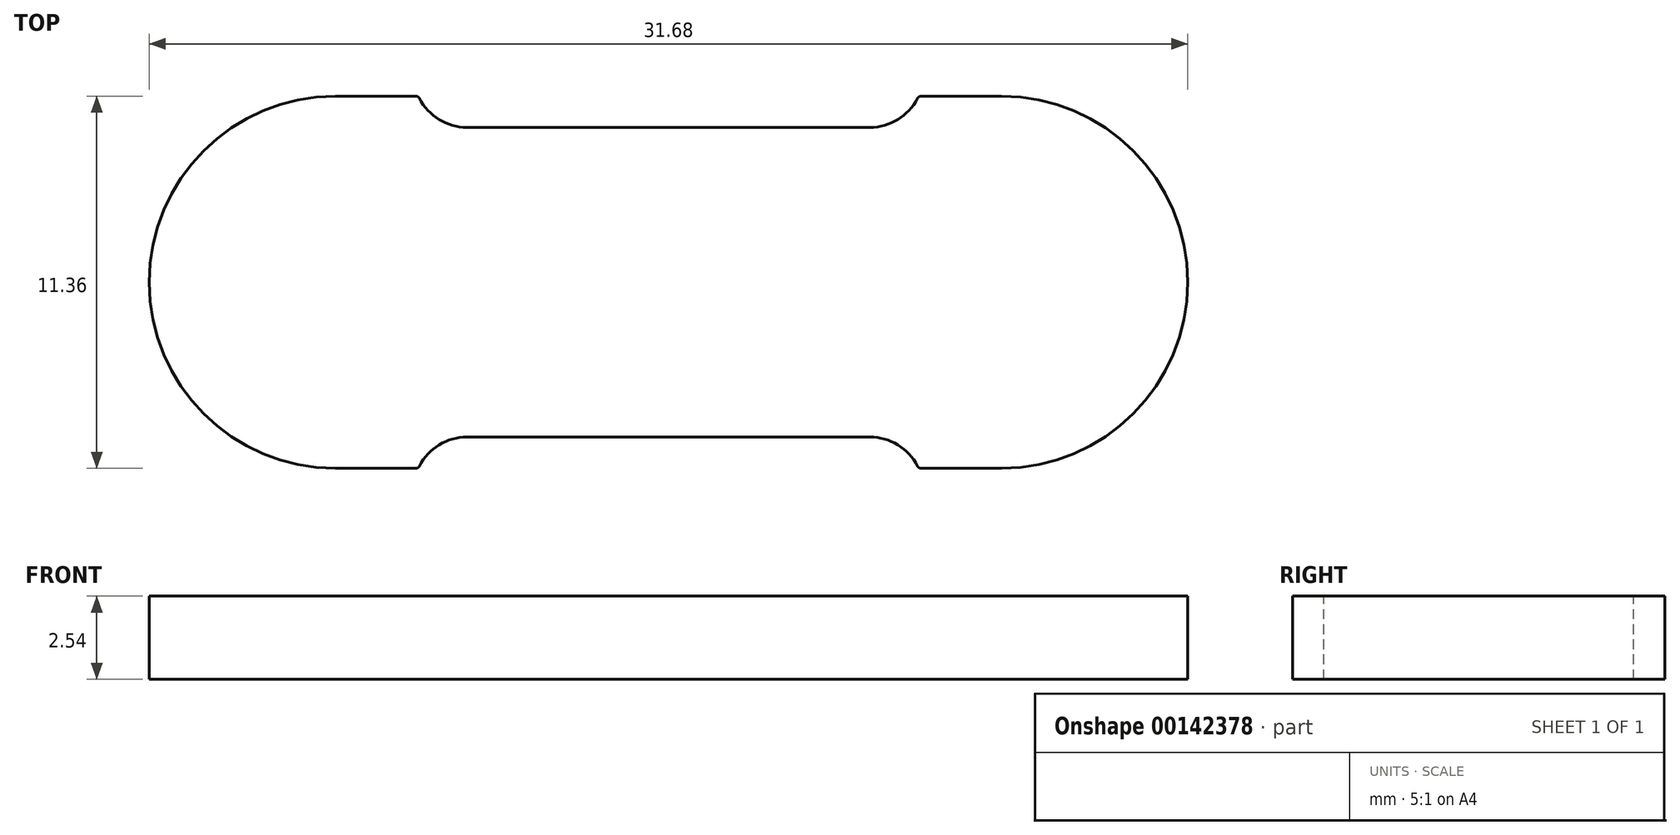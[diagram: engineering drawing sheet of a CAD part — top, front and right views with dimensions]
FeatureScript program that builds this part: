
annotation { "Feature Type Name" : "Feature", "Feature Type Description" : "" }
export const myFeature = defineFeature(function(context is Context, id is Id, definition is map)
    precondition{}
    {
        {
            var Q0;
            Q0=qCreatedBy(makeId("Top.planeOp"),FACE);
            var sketch = newSketch(context, id + "F0", { "sketchPlane" : qUnion([Q0])});
            skArc(sketch, "E0", {"start": v(-10.16, 6.31) * mm, "mid": v(-16.47, 0) * mm, "end": v(-10.16, -6.31) * mm});
            skArc(sketch, "E1", {"start": v(10.16, -6.31) * mm, "mid": v(16.47, 0) * mm, "end": v(10.16, 6.31) * mm});
            skLineSegment(sketch, "E2", {"start": v(-12.5, 0) * mm, "end": v(12.5, 0) * mm, "construction": true});
            skLineSegment(sketch, "E3", {"start": v(0, 11.33) * mm, "end": v(0, -10.01) * mm, "construction": true});
            skLineSegment(sketch, "E4.bottom", {"start": v(-6.7, 4.22) * mm, "end": v(6.7, 4.22) * mm});
            skLineSegment(sketch, "E4.top", {"start": v(-6.7, -4.22) * mm, "end": v(6.7, -4.22) * mm});
            skLineSegment(sketch, "E4.left", {"start": v(-6.7, 4.22) * mm, "end": v(-6.7, -4.22) * mm});
            skLineSegment(sketch, "E4.right", {"start": v(6.7, 4.22) * mm, "end": v(6.7, -4.22) * mm});
            skPoint(sketch, "E4.middle", {"position": v(0, 0) * mm});
            skLineSegment(sketch, "E5", {"start": v(-10.16, 6.31) * mm, "end": v(10.16, 6.31) * mm});
            skLineSegment(sketch, "E6", {"start": v(-10.16, -6.31) * mm, "end": v(10.16, -6.31) * mm});
            skLineSegment(sketch, "E7.0", {"start": v(-6.15, 4.72) * mm, "end": v(6.15, 4.72) * mm});
            skLineSegment(sketch, "E8.0", {"start": v(-6.15, -4.72) * mm, "end": v(6.15, -4.72) * mm});
            skLineSegment(sketch, "E9.0", {"start": v(-10.16, 5.68) * mm, "end": v(10.16, 5.68) * mm});
            skArc(sketch, "E9.1", {"start": v(-10.16, 5.68) * mm, "mid": v(-15.84, 0) * mm, "end": v(-10.16, -5.68) * mm});
            skLineSegment(sketch, "E9.2", {"start": v(-10.16, -5.68) * mm, "end": v(10.16, -5.68) * mm});
            skArc(sketch, "E9.3", {"start": v(10.16, -5.68) * mm, "mid": v(15.84, 0) * mm, "end": v(10.16, 5.68) * mm});
            skCircle(sketch, "E10", {"center": v(-6.15, 6.35) * mm, "radius": 1.63 * mm});
            skCircle(sketch, "E11", {"center": v(6.15, 6.35) * mm, "radius": 1.63 * mm});
            skCircle(sketch, "E12", {"center": v(-6.15, -6.35) * mm, "radius": 1.63 * mm});
            skCircle(sketch, "E13", {"center": v(6.15, -6.35) * mm, "radius": 1.63 * mm});
            skSolve(sketch);
        }
        {
            var Q0;
            Q0=makeQuery(id+"F0.imprint","IMPRINT",FACE,{"disambiguationData":[TD([[makeQuery(id+"F0.imprint","IMPRINT",EDGE,{"derivedFrom":sQuery(id+"F0.wireOp",EDGE,"E4.bottom")}),1.0]])]});
            var Q1;
            Q1=makeQuery(id+"F0.imprint","IMPRINT",FACE,{"disambiguationData":[TD([[makeQuery(id+"F0.imprint","IMPRINT",EDGE,{"derivedFrom":sQuery(id+"F0.wireOp",EDGE,"E4.bottom")}),-1.0]])]});
            extrude(context, id + "F1", {"entities" : qUnion([Q0, Q1]), "oppositeDirection" : true, "depth" : 2.54 * mm});
        }
        {
            var Q0;
            Q0=makeQuery(id+"F1.opExtrude","SWEPT_EDGE",EDGE,{"disambiguationData":[OSD([sQuery(id+"F0.wireOp",EDGE,"E9.0"),sQuery(id+"F0.wireOp",EDGE,"E10")])]});
            var Q1;
            Q1=makeQuery(id+"F1.opExtrude","SWEPT_EDGE",EDGE,{"disambiguationData":[OSD([sQuery(id+"F0.wireOp",EDGE,"E9.0"),sQuery(id+"F0.wireOp",EDGE,"E11")])]});
            var Q2;
            Q2=makeQuery(id+"F1.opExtrude","SWEPT_EDGE",EDGE,{"disambiguationData":[OSD([sQuery(id+"F0.wireOp",EDGE,"E9.2"),sQuery(id+"F0.wireOp",EDGE,"E13")])]});
            var Q3;
            Q3=makeQuery(id+"F1.opExtrude","SWEPT_EDGE",EDGE,{"disambiguationData":[OSD([sQuery(id+"F0.wireOp",EDGE,"E9.2"),sQuery(id+"F0.wireOp",EDGE,"E12")])]});
            fillet(context, id + "F2", {"entities" : qUnion([Q0, Q1, Q2, Q3]), "radius" : 0.13 * mm, "tangentPropagation" : true, "allowEdgeOverflow" : false});
        }
    });
